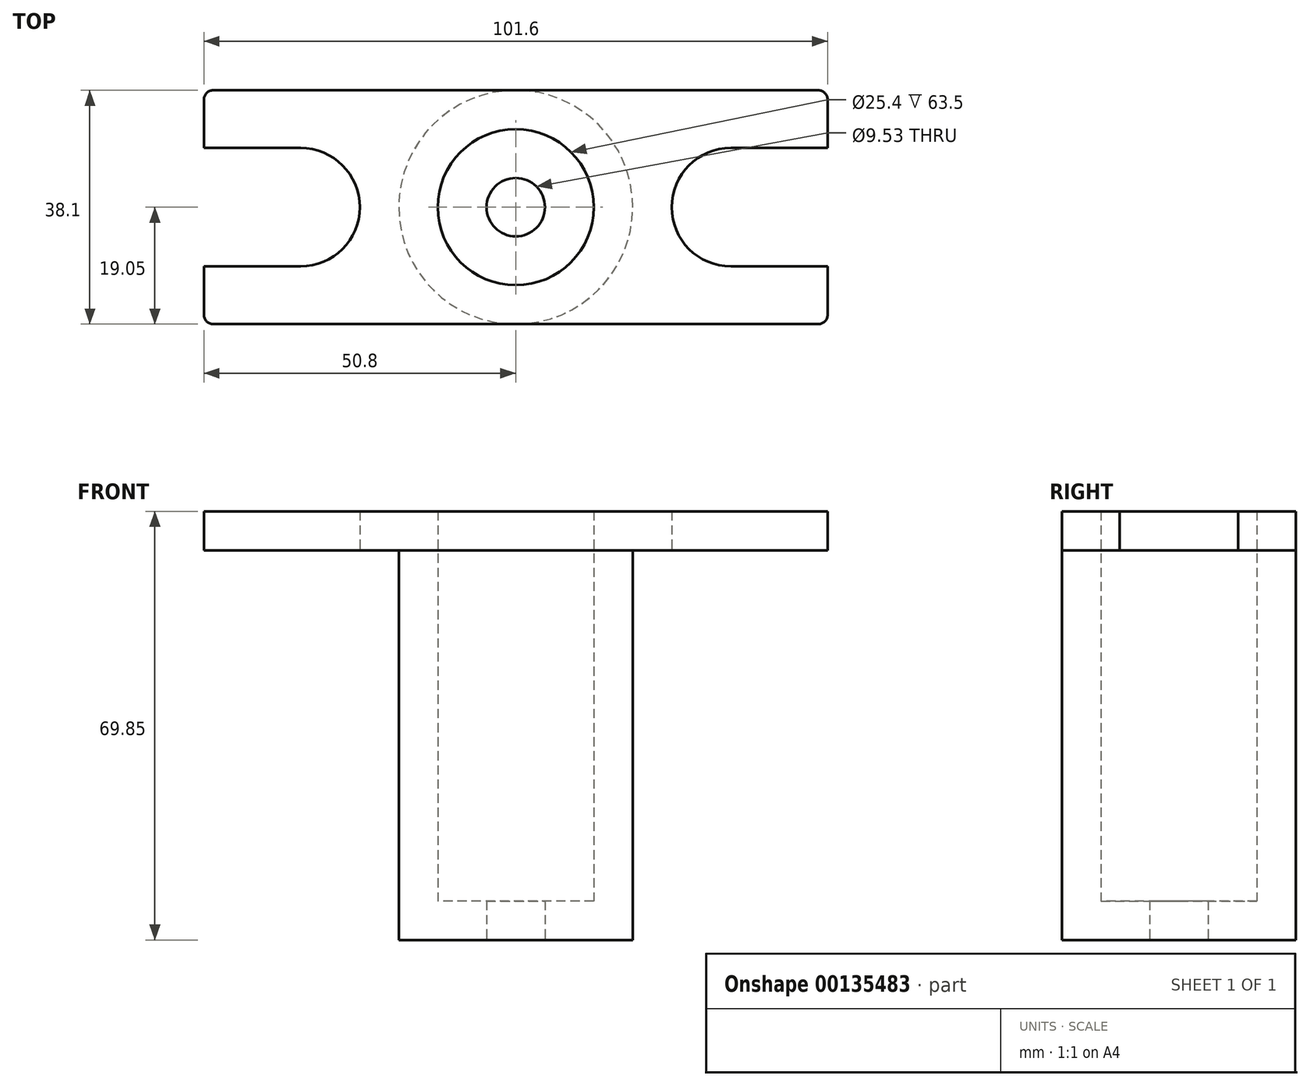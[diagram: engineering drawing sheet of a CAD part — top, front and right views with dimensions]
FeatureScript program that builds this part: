
annotation { "Feature Type Name" : "Feature", "Feature Type Description" : "" }
export const myFeature = defineFeature(function(context is Context, id is Id, definition is map)
    precondition{}
    {
        {
            var Q0;
            Q0=qCreatedBy(makeId("Top.planeOp"),FACE);
            var sketch = newSketch(context, id + "F0", { "sketchPlane" : qUnion([Q0])});
            skLineSegment(sketch, "E0.bottom", {"start": v(0, 0) * mm, "end": v(101.6, 0) * mm});
            skLineSegment(sketch, "E0.top", {"start": v(0, 38.1) * mm, "end": v(101.6, 38.1) * mm});
            skLineSegment(sketch, "E0.left", {"start": v(0, 0) * mm, "end": v(0, 9.4) * mm});
            skLineSegment(sketch, "E0.right", {"start": v(101.6, 0) * mm, "end": v(101.6, 9.4) * mm});
            skLineSegment(sketch, "E1", {"start": v(101.6, 28.7) * mm, "end": v(85.85, 28.7) * mm});
            skLineSegment(sketch, "E2", {"start": v(101.6, 9.4) * mm, "end": v(85.85, 9.4) * mm});
            skArc(sketch, "E3", {"start": v(85.85, 28.7) * mm, "mid": v(76.2, 19.05) * mm, "end": v(85.85, 9.4) * mm});
            skLineSegment(sketch, "E4.trimOffspring", {"start": v(101.6, 28.7) * mm, "end": v(101.6, 38.1) * mm});
            skPoint(sketch, "E5.centerSnap0", {"position": v(0, 19.05) * mm});
            skPoint(sketch, "E5.centerSnap1", {"position": v(50.8, 38.1) * mm});
            skCircle(sketch, "E6", {"center": v(50.8, 19.05) * mm, "radius": 12.7 * mm});
            skLineSegment(sketch, "E7", {"start": v(0, 19.05) * mm, "end": v(85.85, 19.05) * mm, "construction": true});
            skLineSegment(sketch, "E8", {"start": v(50.8, 38.1) * mm, "end": v(50.8, 0) * mm, "construction": true});
            skArc(sketch, "E9.MirrorCS", {"start": v(15.75, 28.7) * mm, "mid": v(25.4, 19.05) * mm, "end": v(15.75, 9.4) * mm});
            skLineSegment(sketch, "E10.MirrorCS", {"start": v(0, 28.7) * mm, "end": v(15.75, 28.7) * mm});
            skLineSegment(sketch, "E11.MirrorCS", {"start": v(0, 9.4) * mm, "end": v(15.75, 9.4) * mm});
            skLineSegment(sketch, "E12.trimOffspring", {"start": v(0, 28.7) * mm, "end": v(0, 38.1) * mm});
            skSolve(sketch);
        }
        {
            var Q0;
            Q0=makeQuery(id+"F0.imprint","IMPRINT",FACE,{"disambiguationData":[TD([[makeQuery(id+"F0.imprint","IMPRINT",EDGE,{"derivedFrom":sQuery(id+"F0.wireOp",EDGE,"E0.bottom")}),1.0]])]});
            extrude(context, id + "F1", {"entities" : qUnion([Q0]), "depth" : 6.35 * mm});
        }
        {
            var Q0;
            Q0=makeQuery(id+"F1.opExtrude","CAP_FACE",FACE,{"disambiguationData":[OSD([sQuery(id+"F0.wireOp",EDGE,"E0.bottom"),sQuery(id+"F0.wireOp",EDGE,"E0.top"),sQuery(id+"F0.wireOp",EDGE,"E0.left"),sQuery(id+"F0.wireOp",EDGE,"E0.right"),sQuery(id+"F0.wireOp",EDGE,"E1"),sQuery(id+"F0.wireOp",EDGE,"E2"),sQuery(id+"F0.wireOp",EDGE,"E3"),sQuery(id+"F0.wireOp",EDGE,"E4.trimOffspring"),sQuery(id+"F0.wireOp",EDGE,"E6"),sQuery(id+"F0.wireOp",EDGE,"E9.MirrorCS"),sQuery(id+"F0.wireOp",EDGE,"E10.MirrorCS"),sQuery(id+"F0.wireOp",EDGE,"E11.MirrorCS"),sQuery(id+"F0.wireOp",EDGE,"E12.trimOffspring")])],"isStart":false});
            var sketch = newSketch(context, id + "F2", { "sketchPlane" : qUnion([Q0])});
            skCircle(sketch, "E13", {"center": v(50.8, 19.05) * mm, "radius": 12.7 * mm});
            skCircle(sketch, "E14", {"center": v(50.8, 19.05) * mm, "radius": 19.05 * mm});
            skSolve(sketch);
        }
        {
            var Q0;
            Q0=makeQuery(id+"F2.imprint","IMPRINT",FACE,{"disambiguationData":[TD([[makeQuery(id+"F2.imprint","IMPRINT",EDGE,{"derivedFrom":sQuery(id+"F2.wireOp",EDGE,"E13")}),-1.0]])]});
            extrude(context, id + "F3", {"entities" : qUnion([Q0]), "operationType" : NewBodyOperationType.ADD, "oppositeDirection" : true, "depth" : 69.85 * mm});
        }
        {
            var Q0;
            Q0=makeQuery(id+"F3.opExtrude","CAP_FACE",FACE,{"disambiguationData":[OSD([sQuery(id+"F2.wireOp",EDGE,"E13"),sQuery(id+"F2.wireOp",EDGE,"E14")])],"isStart":false});
            var sketch = newSketch(context, id + "F4", { "sketchPlane" : qUnion([Q0])});
            skCircle(sketch, "E15", {"center": v(50.8, -19.05) * mm, "radius": 12.7 * mm});
            skCircle(sketch, "E16", {"center": v(50.8, -19.05) * mm, "radius": 19.05 * mm});
            skCircle(sketch, "E17", {"center": v(50.8, -19.05) * mm, "radius": 4.76 * mm});
            skSolve(sketch);
        }
        {
            var Q0;
            Q0=makeQuery(id+"F4.imprint","IMPRINT",FACE,{"disambiguationData":[TD([[makeQuery(id+"F4.imprint","IMPRINT",EDGE,{"derivedFrom":sQuery(id+"F4.wireOp",EDGE,"E15")}),-1.0]])]});
            extrude(context, id + "F5", {"entities" : qUnion([Q0]), "operationType" : NewBodyOperationType.ADD, "oppositeDirection" : true, "depth" : 6.35 * mm});
        }
        {
            var Q0;
            Q0=makeQuery(id+"F1.opExtrude","SWEPT_EDGE",EDGE,{"disambiguationData":[OSD([sQuery(id+"F0.wireOp",EDGE,"E0.bottom"),sQuery(id+"F0.wireOp",EDGE,"E0.right")])]});
            var Q1;
            Q1=makeQuery(id+"F1.opExtrude","SWEPT_EDGE",EDGE,{"disambiguationData":[OSD([sQuery(id+"F0.wireOp",EDGE,"E0.top"),sQuery(id+"F0.wireOp",EDGE,"E4.trimOffspring")])]});
            var Q2;
            Q2=makeQuery(id+"F1.opExtrude","SWEPT_EDGE",EDGE,{"disambiguationData":[OSD([sQuery(id+"F0.wireOp",EDGE,"E0.bottom"),sQuery(id+"F0.wireOp",EDGE,"E0.left")])]});
            var Q3;
            Q3=makeQuery(id+"F1.opExtrude","SWEPT_EDGE",EDGE,{"disambiguationData":[OSD([sQuery(id+"F0.wireOp",EDGE,"E0.top"),sQuery(id+"F0.wireOp",EDGE,"E12.trimOffspring")])]});
            fillet(context, id + "F6", {"entities" : qUnion([Q0, Q1, Q2, Q3]), "radius" : 1.52 * mm, "tangentPropagation" : true, "allowEdgeOverflow" : false});
        }
    });
